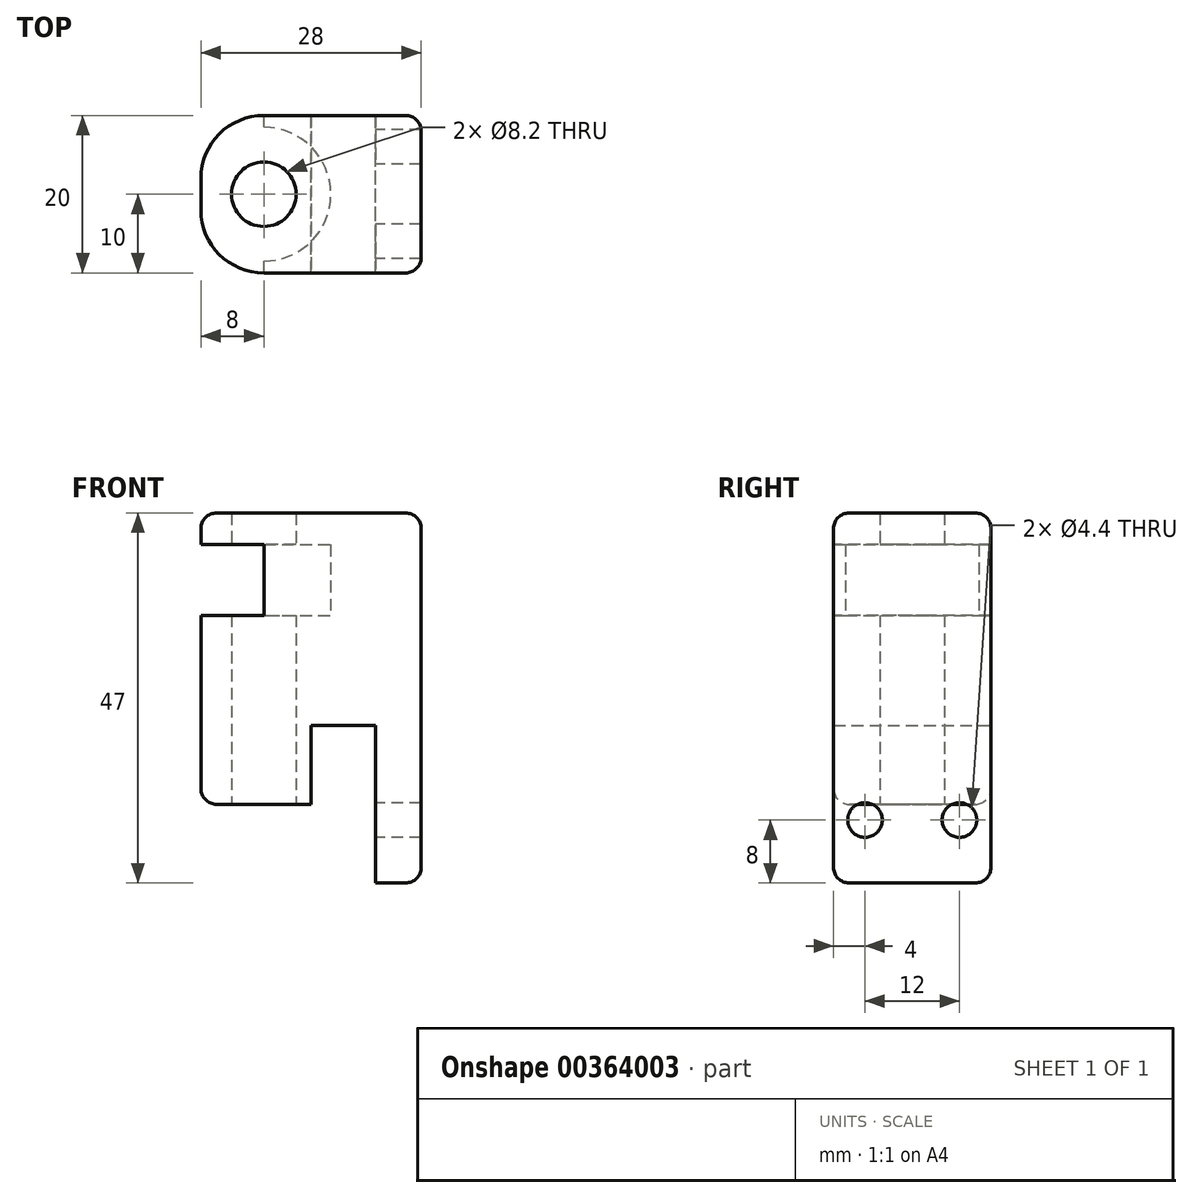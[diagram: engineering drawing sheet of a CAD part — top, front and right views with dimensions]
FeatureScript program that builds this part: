
annotation { "Feature Type Name" : "Feature", "Feature Type Description" : "" }
export const myFeature = defineFeature(function(context is Context, id is Id, definition is map)
    precondition{}
    {
        {
            var Q0;
            Q0=qCreatedBy(makeId("Top.planeOp"),FACE);
            var sketch = newSketch(context, id + "F0", { "sketchPlane" : qUnion([Q0])});
            skLineSegment(sketch, "E0.bottom", {"start": v(0, -10) * mm, "end": v(20, -10) * mm});
            skLineSegment(sketch, "E0.top", {"start": v(0, 10) * mm, "end": v(20, 10) * mm});
            skLineSegment(sketch, "E0.right", {"start": v(20, -10) * mm, "end": v(20, 10) * mm});
            skLineSegment(sketch, "E1", {"start": v(0, 0) * mm, "end": v(-5, 0) * mm, "construction": true});
            skCircle(sketch, "E2", {"center": v(0, 0) * mm, "radius": 4.1 * mm});
            skArc(sketch, "E3", {"start": v(0, 10) * mm, "mid": v(-5.66, 7.66) * mm, "end": v(-8, 2) * mm});
            skLineSegment(sketch, "E4", {"start": v(-8, 2) * mm, "end": v(-8, -2) * mm});
            skArc(sketch, "E5", {"start": v(0, -10) * mm, "mid": v(-5.66, -7.66) * mm, "end": v(-8, -2) * mm});
            skSolve(sketch);
        }
        {
            var Q0;
            Q0=qSketchRegion(id+"F0",true);
            extrude(context, id + "F1", {"entities" : qUnion([Q0]), "depth" : 34 * mm, "offsetDistance" : 25 * mm});
        }
        {
            var Q0;
            Q0=makeQuery(id+"F1.opExtrude","CAP_FACE",FACE,{"disambiguationData":[OSD([sQuery(id+"F0.wireOp",EDGE,"E0.bottom"),sQuery(id+"F0.wireOp",EDGE,"E0.top"),sQuery(id+"F0.wireOp",EDGE,"E0.left"),sQuery(id+"F0.wireOp",EDGE,"E0.right"),sQuery(id+"F0.wireOp",EDGE,"E2"),sQuery(id+"F0.wireOp",EDGE,"4TDl4ayu-9JZQ-zShW-qO7n-mEqhDuUFqM36"),sQuery(id+"F0.wireOp",EDGE,"nupkRt8J-H5qi-5iNm-krWY-gsQpabFCNbI2"),sQuery(id+"F0.wireOp",EDGE,"lVVR2pLq-n3Sc-anlP-BnDX-gxRU0PT0zg8c")])],"isStart":false});
            var sketch = newSketch(context, id + "F2", { "sketchPlane" : qUnion([Q0])});
            skArc(sketch, "E6", {"start": v(0, 8.5) * mm, "mid": v(8.5, 0) * mm, "end": v(0, -8.5) * mm});
            skLineSegment(sketch, "E7", {"start": v(0, 8.5) * mm, "end": v(0, 10) * mm});
            skLineSegment(sketch, "E8", {"start": v(0, 10) * mm, "end": v(20, 10) * mm});
            skLineSegment(sketch, "E9", {"start": v(20, 10) * mm, "end": v(20, -10) * mm});
            skLineSegment(sketch, "E10", {"start": v(20, -10) * mm, "end": v(0, -10) * mm});
            skLineSegment(sketch, "E11", {"start": v(0, -10) * mm, "end": v(0, -8.5) * mm});
            skSolve(sketch);
        }
        {
            var Q0;
            Q0=qSketchRegion(id+"F2",true);
            extrude(context, id + "F3", {"entities" : qUnion([Q0]), "operationType" : NewBodyOperationType.ADD, "depth" : 9 * mm, "offsetDistance" : 25 * mm});
        }
        {
            var Q0;
            Q0=makeQuery(id+"F3.opExtrude","CAP_FACE",FACE,{"disambiguationData":[OSD([sQuery(id+"F2.wireOp",EDGE,"E6"),sQuery(id+"F2.wireOp",EDGE,"E7"),sQuery(id+"F2.wireOp",EDGE,"E8"),sQuery(id+"F2.wireOp",EDGE,"E9"),sQuery(id+"F2.wireOp",EDGE,"E10"),sQuery(id+"F2.wireOp",EDGE,"E11"),sQuery(id+"F2.wireOp",EDGE,"l3wCq06U-No4X-bPcO-I9yK-p1roc5aXHv7O"),sQuery(id+"F2.wireOp",EDGE,"rE4ebA5y-rJy4-s34L-vENf-2cb6GeVkQMQO"),sQuery(id+"F2.wireOp",EDGE,"jQMfOj7b-nA0K-HmRX-XfbD-jgQkhQMTI5OJ")])],"isStart":false});
            var sketch = newSketch(context, id + "F4", { "sketchPlane" : qUnion([Q0])});
            skLineSegment(sketch, "E12.bottom", {"start": v(20, 10) * mm, "end": v(0, 10) * mm});
            skLineSegment(sketch, "E12.top", {"start": v(20, -10) * mm, "end": v(0, -10) * mm});
            skLineSegment(sketch, "E12.left", {"start": v(20, 10) * mm, "end": v(20, -10) * mm});
            skCircle(sketch, "E13", {"center": v(0, 0) * mm, "radius": 4.1 * mm});
            skArc(sketch, "E14", {"start": v(0, 10) * mm, "mid": v(-5.66, 7.66) * mm, "end": v(-8, 2) * mm});
            skArc(sketch, "E15", {"start": v(0, -10) * mm, "mid": v(-5.66, -7.66) * mm, "end": v(-8, -2) * mm});
            skLineSegment(sketch, "E16", {"start": v(-8, -2) * mm, "end": v(-8, 2) * mm});
            skSolve(sketch);
        }
        {
            var Q0;
            Q0=qSketchRegion(id+"F4",true);
            extrude(context, id + "F5", {"entities" : qUnion([Q0]), "operationType" : NewBodyOperationType.ADD, "depth" : 4 * mm, "offsetDistance" : 25 * mm});
        }
        {
            var Q0;
            Q0=makeQuery(id+"F1.opExtrude","CAP_FACE",FACE,{"disambiguationData":[OSD([sQuery(id+"F0.wireOp",EDGE,"E0.bottom"),sQuery(id+"F0.wireOp",EDGE,"E0.top"),sQuery(id+"F0.wireOp",EDGE,"E0.right"),sQuery(id+"F0.wireOp",EDGE,"E2"),sQuery(id+"F0.wireOp",EDGE,"E3"),sQuery(id+"F0.wireOp",EDGE,"E4"),sQuery(id+"F0.wireOp",EDGE,"E5")])],"isStart":true});
            var sketch = newSketch(context, id + "F6", { "sketchPlane" : qUnion([Q0])});
            skLineSegment(sketch, "E17.bottom", {"start": v(6, 10) * mm, "end": v(14.2, 10) * mm});
            skLineSegment(sketch, "E17.top", {"start": v(6, -10) * mm, "end": v(14.2, -10) * mm});
            skLineSegment(sketch, "E17.left", {"start": v(6, 10) * mm, "end": v(6, -10) * mm});
            skLineSegment(sketch, "E17.right", {"start": v(14.2, 10) * mm, "end": v(14.2, -10) * mm});
            skSolve(sketch);
        }
        {
            var Q0;
            Q0=makeQuery(id+"F6.imprint","IMPRINT",FACE,{"disambiguationData":[TD([[makeQuery(id+"F6.imprint","IMPRINT",EDGE,{"derivedFrom":sQuery(id+"F6.wireOp",EDGE,"E17.bottom")}),-1.0]])]});
            extrude(context, id + "F7", {"entities" : qUnion([Q0]), "operationType" : NewBodyOperationType.REMOVE, "oppositeDirection" : true, "depth" : 20 * mm, "offsetDistance" : 25 * mm});
        }
        {
            var Q0;
            {var subQ0=sQuery(id+"F0.wireOp",EDGE,"E5");var subQ1=sQuery(id+"F0.wireOp",EDGE,"E4");var subQ2=sQuery(id+"F0.wireOp",EDGE,"E0.bottom");var subQ3=sQuery(id+"F0.wireOp",EDGE,"E2");var subQ4=sQuery(id+"F0.wireOp",EDGE,"E0.top");var subQ5=sQuery(id+"F0.wireOp",EDGE,"E3");Q0=makeQuery(id+"F7.boolean.opBoolean","SPLIT",FACE,{"disambiguationData":[TD([makeQuery(id+"F1.opExtrude","SWEPT_FACE",FACE,{"disambiguationData":[OSD([subQ3])]})])],"derivedFrom":makeQuery(id+"F1.opExtrude","CAP_FACE",FACE,{"disambiguationData":[OSD([subQ2,subQ4,sQuery(id+"F0.wireOp",EDGE,"E0.right"),subQ3,subQ5,subQ1,subQ0])],"isStart":true})});}
            var sketch = newSketch(context, id + "F8", { "sketchPlane" : qUnion([Q0])});
            skLineSegment(sketch, "E18.bottom", {"start": v(6, -10) * mm, "end": v(-9.19, -10) * mm});
            skLineSegment(sketch, "E18.top", {"start": v(6, 11.66) * mm, "end": v(-9.19, 11.66) * mm});
            skLineSegment(sketch, "E18.left", {"start": v(6, -10) * mm, "end": v(6, 11.66) * mm});
            skLineSegment(sketch, "E18.right", {"start": v(-9.19, -10) * mm, "end": v(-9.19, 11.66) * mm});
            skSolve(sketch);
        }
        {
            var Q0;
            Q0 = qSketchRegion(id + "F8", true);
            extrude(context, id + "F9", {"entities" : qUnion([Q0]), "operationType" : NewBodyOperationType.REMOVE, "oppositeDirection" : true, "depth" : 10 * mm, "offsetDistance" : 25 * mm});
        }
        {
            var Q0;
            Q0=makeQuery(id+"F7.boolean.opBoolean","COPY",FACE,{"derivedFrom":makeQuery(id+"F7.opExtrude","SWEPT_FACE",FACE,{"disambiguationData":[OSD([sQuery(id+"F6.wireOp",EDGE,"E17.right")])]})});
            var sketch = newSketch(context, id + "F10", { "sketchPlane" : qUnion([Q0])});
            skCircle(sketch, "E19", {"center": v(6, 8) * mm, "radius": 2.2 * mm});
            skCircle(sketch, "E20", {"center": v(-6, 8) * mm, "radius": 2.2 * mm});
            skSolve(sketch);
        }
        {
            var Q0;
            Q0 = qSketchRegion(id + "F10", true);
            extrude(context, id + "F11", {"entities" : qUnion([Q0]), "operationType" : NewBodyOperationType.REMOVE, "oppositeDirection" : true, "depth" : 25 * mm, "offsetDistance" : 25 * mm});
        }
        {
            var Q0;
            {var subQ0=sQuery(id+"F0.wireOp",EDGE,"E0.right");var subQ1=sQuery(id+"F0.wireOp",EDGE,"E0.top");Q0=makeQuery(id+"F7.boolean.opBoolean","SPLIT",EDGE,{"disambiguationData":[TD([makeQuery(id+"F1.opExtrude","SWEPT_FACE",FACE,{"disambiguationData":[OSD([subQ0])]})])],"derivedFrom":makeQuery(id+"F1.opExtrude","CAP_EDGE",EDGE,{"disambiguationData":[OSD([subQ1])],"isStart":true})});}
            var Q1;
            Q1=makeQuery(id+"F5.opExtrude","CAP_EDGE",EDGE,{"disambiguationData":[OSD([sQuery(id+"F4.wireOp",EDGE,"E12.bottom")])],"isStart":false});
            var Q2;
            Q2=makeQuery(id+"F5.opExtrude","CAP_EDGE",EDGE,{"disambiguationData":[OSD([sQuery(id+"F4.wireOp",EDGE,"E12.left")])],"isStart":false});
            var Q3;
            Q3=makeQuery(id+"F5.boolean.opBoolean","MERGE",EDGE,{"derivedFrom":[makeQuery(id+"F3.boolean.opBoolean","MERGE",EDGE,{"derivedFrom":[makeQuery(id+"F1.opExtrude","SWEPT_EDGE",EDGE,{"disambiguationData":[OSD([sQuery(id+"F0.wireOp",EDGE,"E0.top"),sQuery(id+"F0.wireOp",EDGE,"E0.right")])]}),makeQuery(id+"F3.opExtrude","SWEPT_EDGE",EDGE,{"disambiguationData":[OSD([sQuery(id+"F2.wireOp",EDGE,"E8"),sQuery(id+"F2.wireOp",EDGE,"E9")])]})]}),makeQuery(id+"F5.opExtrude","SWEPT_EDGE",EDGE,{"disambiguationData":[OSD([sQuery(id+"F4.wireOp",EDGE,"E12.bottom"),sQuery(id+"F4.wireOp",EDGE,"E12.left")])]})]});
            var Q4;
            Q4=makeQuery(id+"F5.boolean.opBoolean","MERGE",EDGE,{"derivedFrom":[makeQuery(id+"F3.boolean.opBoolean","MERGE",EDGE,{"derivedFrom":[makeQuery(id+"F1.opExtrude","SWEPT_EDGE",EDGE,{"disambiguationData":[OSD([sQuery(id+"F0.wireOp",EDGE,"E0.bottom"),sQuery(id+"F0.wireOp",EDGE,"E0.right")])]}),makeQuery(id+"F3.opExtrude","SWEPT_EDGE",EDGE,{"disambiguationData":[OSD([sQuery(id+"F2.wireOp",EDGE,"E9"),sQuery(id+"F2.wireOp",EDGE,"E10")])]})]}),makeQuery(id+"F5.opExtrude","SWEPT_EDGE",EDGE,{"disambiguationData":[OSD([sQuery(id+"F4.wireOp",EDGE,"E12.top"),sQuery(id+"F4.wireOp",EDGE,"E12.left")])]})]});
            var Q5;
            Q5=makeQuery(id+"F1.opExtrude","CAP_EDGE",EDGE,{"disambiguationData":[OSD([sQuery(id+"F0.wireOp",EDGE,"E0.right")])],"isStart":true});
            var Q6;
            {var subQ0=sQuery(id+"F0.wireOp",EDGE,"E0.right");var subQ1=sQuery(id+"F0.wireOp",EDGE,"E0.bottom");Q6=makeQuery(id+"F7.boolean.opBoolean","SPLIT",EDGE,{"disambiguationData":[TD([makeQuery(id+"F1.opExtrude","SWEPT_FACE",FACE,{"disambiguationData":[OSD([subQ0])]})])],"derivedFrom":makeQuery(id+"F1.opExtrude","CAP_EDGE",EDGE,{"disambiguationData":[OSD([subQ1])],"isStart":true})});}
            var Q7;
            Q7=makeQuery(id+"F9.boolean.opBoolean","INTERSECT",EDGE,{"derivedFrom":[makeQuery(id+"F1.opExtrude","SWEPT_FACE",FACE,{"disambiguationData":[OSD([sQuery(id+"F0.wireOp",EDGE,"E5")])]}),makeQuery(id+"F9.opExtrude","CAP_FACE",FACE,{"disambiguationData":[OSD([sQuery(id+"F8.wireOp",EDGE,"E18.bottom"),sQuery(id+"F8.wireOp",EDGE,"E18.top"),sQuery(id+"F8.wireOp",EDGE,"E18.left"),sQuery(id+"F8.wireOp",EDGE,"E18.right")])],"isStart":false})]});
            fillet(context, id + "F12", {"entities" : qUnion([Q0, Q1, Q2, Q3, Q4, Q5, Q6, Q7]), "radius" : 2 * mm, "tangentPropagation" : true, "allowEdgeOverflow" : false});
        }
    });
